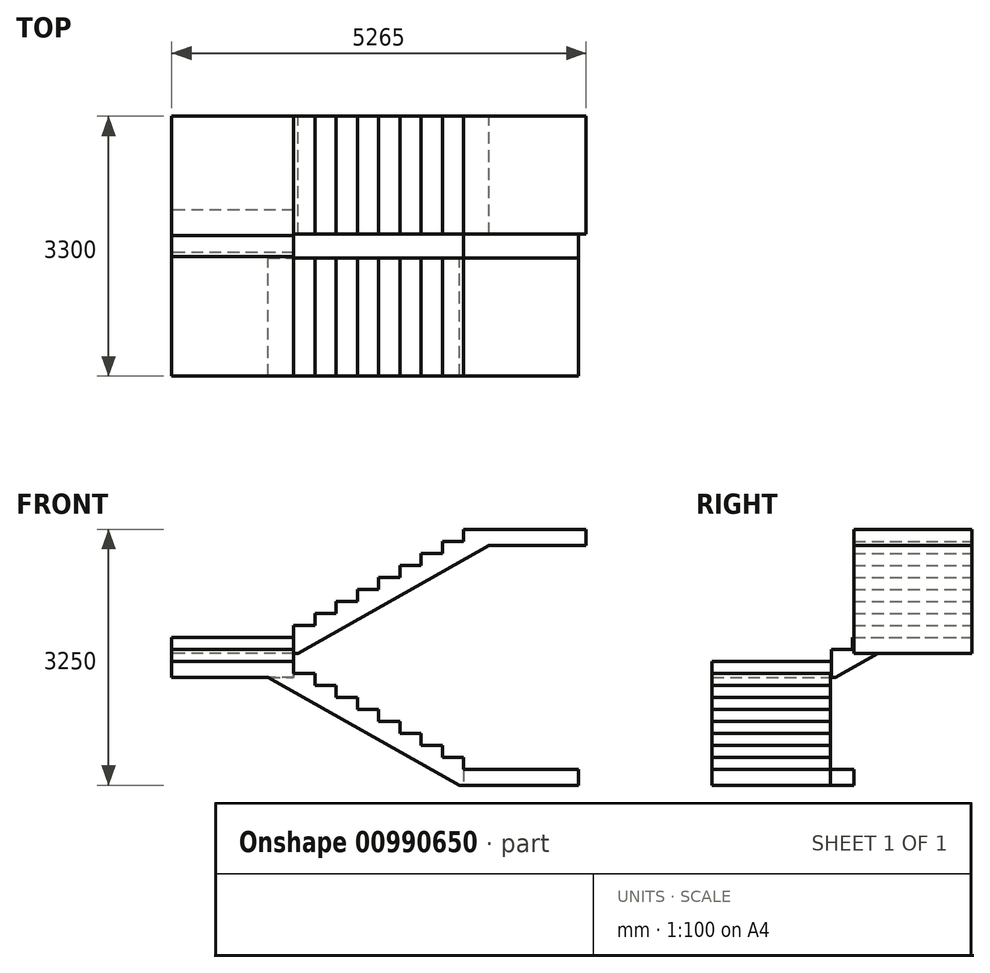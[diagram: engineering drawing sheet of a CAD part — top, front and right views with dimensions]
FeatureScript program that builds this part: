
annotation { "Feature Type Name" : "Feature", "Feature Type Description" : "" }
export const myFeature = defineFeature(function(context is Context, id is Id, definition is map)
    precondition{}
    {
        {
            var Q0;
            Q0=qCreatedBy(makeId("Front.planeOp"),FACE);
            var sketch = newSketch(context, id + "F0", { "sketchPlane" : qUnion([Q0])});
            skLineSegment(sketch, "E0", {"start": v(-2899.3, -2094.7) * mm, "end": v(-1349.3, -2094.7) * mm});
            skLineSegment(sketch, "E1", {"start": v(-1349.3, -2094.7) * mm, "end": v(-1349.3, -2247.2) * mm});
            skLineSegment(sketch, "E2", {"start": v(-1349.3, -2247.2) * mm, "end": v(-1079.3, -2247.2) * mm});
            skLineSegment(sketch, "E3", {"start": v(-1079.3, -2247.2) * mm, "end": v(-1079.3, -2399.7) * mm});
            skLineSegment(sketch, "E4", {"start": v(-1079.3, -2399.7) * mm, "end": v(-809.3, -2399.7) * mm});
            skLineSegment(sketch, "E5", {"start": v(-809.3, -2399.7) * mm, "end": v(-809.3, -2552.2) * mm});
            skLineSegment(sketch, "E6", {"start": v(-809.3, -2552.2) * mm, "end": v(-539.3, -2552.2) * mm});
            skLineSegment(sketch, "E7", {"start": v(-539.3, -2552.2) * mm, "end": v(-539.3, -2704.7) * mm});
            skLineSegment(sketch, "E8", {"start": v(-539.3, -2704.7) * mm, "end": v(-269.3, -2704.7) * mm});
            skLineSegment(sketch, "E9", {"start": v(-269.3, -2704.7) * mm, "end": v(-269.3, -2857.2) * mm});
            skLineSegment(sketch, "E10", {"start": v(-269.3, -2857.2) * mm, "end": v(0.7, -2857.2) * mm});
            skLineSegment(sketch, "E11", {"start": v(0.7, -2857.2) * mm, "end": v(0.7, -3009.7) * mm});
            skLineSegment(sketch, "E12", {"start": v(0.7, -3009.7) * mm, "end": v(270.7, -3009.7) * mm});
            skLineSegment(sketch, "E13", {"start": v(270.7, -3009.7) * mm, "end": v(270.7, -3162.2) * mm});
            skLineSegment(sketch, "E14", {"start": v(270.7, -3162.2) * mm, "end": v(540.7, -3162.2) * mm});
            skLineSegment(sketch, "E15", {"start": v(540.7, -3162.2) * mm, "end": v(540.7, -3314.7) * mm});
            skLineSegment(sketch, "E16", {"start": v(540.7, -3314.7) * mm, "end": v(810.7, -3314.7) * mm});
            skLineSegment(sketch, "E17", {"start": v(810.7, -3314.7) * mm, "end": v(810.7, -3467.2) * mm});
            skLineSegment(sketch, "E18", {"start": v(810.7, -3467.2) * mm, "end": v(2265.7, -3467.2) * mm});
            skLineSegment(sketch, "E19", {"start": v(2265.7, -3467.2) * mm, "end": v(2265.7, -3667.2) * mm});
            skLineSegment(sketch, "E20", {"start": v(-2899.3, -2094.7) * mm, "end": v(-2899.3, -2294.7) * mm});
            skLineSegment(sketch, "E21.0", {"start": v(-1447.65, -2421.35) * mm, "end": v(712.35, -3641.35) * mm});
            skLineSegment(sketch, "E22", {"start": v(2265.7, -3667.2) * mm, "end": v(758.13, -3667.2) * mm});
            skLineSegment(sketch, "E23", {"start": v(-2899.3, -2294.7) * mm, "end": v(-1671.87, -2294.7) * mm});
            skLineSegment(sketch, "E24", {"start": v(-1447.65, -2421.35) * mm, "end": v(-1671.87, -2294.7) * mm});
            skLineSegment(sketch, "E25", {"start": v(712.35, -3641.35) * mm, "end": v(758.13, -3667.2) * mm});
            skSolve(sketch);
        }
        {
            var Q0;
            Q0=makeQuery(id+"F0.imprint","IMPRINT",FACE,{"disambiguationData":[TD([[makeQuery(id+"F0.imprint","IMPRINT",EDGE,{"derivedFrom":sQuery(id+"F0.wireOp",EDGE,"E0")}),-1.0]])]});
            extrude(context, id + "F1", {"entities" : qUnion([Q0]), "depth" : 1500 * mm, "offsetDistance" : 25 * mm});
        }
        {
            var Q0;
            Q0=makeQuery(id+"F1.opExtrude","CAP_FACE",FACE,{"disambiguationData":[OSD([sQuery(id+"F0.wireOp",EDGE,"E0"),sQuery(id+"F0.wireOp",EDGE,"E1"),sQuery(id+"F0.wireOp",EDGE,"E2"),sQuery(id+"F0.wireOp",EDGE,"E3"),sQuery(id+"F0.wireOp",EDGE,"E4"),sQuery(id+"F0.wireOp",EDGE,"E5"),sQuery(id+"F0.wireOp",EDGE,"E6"),sQuery(id+"F0.wireOp",EDGE,"E7"),sQuery(id+"F0.wireOp",EDGE,"E8"),sQuery(id+"F0.wireOp",EDGE,"E9"),sQuery(id+"F0.wireOp",EDGE,"E10"),sQuery(id+"F0.wireOp",EDGE,"E11"),sQuery(id+"F0.wireOp",EDGE,"E12"),sQuery(id+"F0.wireOp",EDGE,"E13"),sQuery(id+"F0.wireOp",EDGE,"E14"),sQuery(id+"F0.wireOp",EDGE,"E15"),sQuery(id+"F0.wireOp",EDGE,"E16"),sQuery(id+"F0.wireOp",EDGE,"E17"),sQuery(id+"F0.wireOp",EDGE,"E18"),sQuery(id+"F0.wireOp",EDGE,"E19"),sQuery(id+"F0.wireOp",EDGE,"E20"),sQuery(id+"F0.wireOp",EDGE,"E21.0"),sQuery(id+"F0.wireOp",EDGE,"E22"),sQuery(id+"F0.wireOp",EDGE,"E23"),sQuery(id+"F0.wireOp",EDGE,"E24"),sQuery(id+"F0.wireOp",EDGE,"E25")])],"isStart":true});
            var sketch = newSketch(context, id + "F2", { "sketchPlane" : qUnion([Q0])});
            skLineSegment(sketch, "E26", {"start": v(1671.87, -2294.7) * mm, "end": v(1349.3, -2294.7) * mm});
            skLineSegment(sketch, "E27", {"start": v(1349.3, -2294.7) * mm, "end": v(1349.3, -2247.2) * mm});
            skLineSegment(sketch, "E28", {"start": v(1349.3, -2247.2) * mm, "end": v(1349.3, -2094.7) * mm});
            skLineSegment(sketch, "E29", {"start": v(1349.3, -2094.7) * mm, "end": v(2899.3, -2094.7) * mm});
            skLineSegment(sketch, "E30", {"start": v(2899.3, -2094.7) * mm, "end": v(2899.3, -2294.7) * mm});
            skLineSegment(sketch, "E31", {"start": v(2899.3, -2294.7) * mm, "end": v(1671.87, -2294.7) * mm});
            skSolve(sketch);
        }
        {
            var Q0;
            Q0=makeQuery(id+"F2.imprint","IMPRINT",FACE,{"disambiguationData":[TD([[makeQuery(id+"F2.imprint","IMPRINT",EDGE,{"derivedFrom":sQuery(id+"F2.wireOp",EDGE,"E26")}),-1.0]])]});
            extrude(context, id + "F3", {"entities" : qUnion([Q0]), "operationType" : NewBodyOperationType.ADD, "depth" : 15 * mm, "offsetDistance" : 25 * mm});
        }
        {
            var Q0;
            Q0=makeQuery(id+"F3.boolean.opBoolean","MERGE",FACE,{"derivedFrom":[makeQuery(id+"F1.opExtrude","SWEPT_FACE",FACE,{"disambiguationData":[OSD([sQuery(id+"F0.wireOp",EDGE,"E20")])]}),makeQuery(id+"F3.opExtrude","SWEPT_FACE",FACE,{"disambiguationData":[OSD([sQuery(id+"F2.wireOp",EDGE,"E30")])]})]});
            var sketch = newSketch(context, id + "F4", { "sketchPlane" : qUnion([Q0])});
            skLineSegment(sketch, "E32", {"start": v(-15, -2094.7) * mm, "end": v(-15, -1942.2) * mm});
            skLineSegment(sketch, "E33", {"start": v(-15, -1942.2) * mm, "end": v(-285, -1942.2) * mm});
            skLineSegment(sketch, "E34", {"start": v(-285, -1942.2) * mm, "end": v(-285, -1789.7) * mm});
            skLineSegment(sketch, "E35", {"start": v(-285, -1789.7) * mm, "end": v(-1800, -1789.7) * mm});
            skLineSegment(sketch, "E36", {"start": v(-1800, -1789.7) * mm, "end": v(-1800, -1989.7) * mm});
            skLineSegment(sketch, "E37", {"start": v(-1800, -1989.7) * mm, "end": v(-607.58, -1989.7) * mm});
            skLineSegment(sketch, "E38.0", {"start": v(-67.58, -2294.7) * mm, "end": v(-607.58, -1989.7) * mm});
            skLineSegment(sketch, "E39", {"start": v(-15, -2094.7) * mm, "end": v(-15, -2294.7) * mm});
            skLineSegment(sketch, "E40", {"start": v(-15, -2294.7) * mm, "end": v(-67.58, -2294.7) * mm});
            skSolve(sketch);
        }
        {
            var Q0;
            Q0=makeQuery(id+"F4.imprint","IMPRINT",FACE,{"disambiguationData":[TD([[makeQuery(id+"F4.imprint","IMPRINT",EDGE,{"derivedFrom":sQuery(id+"F4.wireOp",EDGE,"E32")}),1.0]])]});
            extrude(context, id + "F5", {"entities" : qUnion([Q0]), "oppositeDirection" : true, "depth" : 1550 * mm, "offsetDistance" : 25 * mm});
        }
        {
            var Q0;
            Q0=makeQuery(id+"F5.opExtrude","SWEPT_FACE",FACE,{"disambiguationData":[OSD([sQuery(id+"F4.wireOp",EDGE,"E36")])]});
            var sketch = newSketch(context, id + "F6", { "sketchPlane" : qUnion([Q0])});
            skLineSegment(sketch, "E41", {"start": v(1349.3, -1789.7) * mm, "end": v(1349.3, -1637.2) * mm});
            skLineSegment(sketch, "E42", {"start": v(1349.3, -1637.2) * mm, "end": v(1079.3, -1637.2) * mm});
            skLineSegment(sketch, "E43", {"start": v(1079.3, -1637.2) * mm, "end": v(1079.3, -1484.7) * mm});
            skLineSegment(sketch, "E44", {"start": v(1079.3, -1484.7) * mm, "end": v(809.3, -1484.7) * mm});
            skLineSegment(sketch, "E45", {"start": v(809.3, -1484.7) * mm, "end": v(809.3, -1332.2) * mm});
            skLineSegment(sketch, "E46", {"start": v(809.3, -1332.2) * mm, "end": v(539.3, -1332.2) * mm});
            skLineSegment(sketch, "E47", {"start": v(539.3, -1332.2) * mm, "end": v(539.3, -1179.7) * mm});
            skLineSegment(sketch, "E48", {"start": v(539.3, -1179.7) * mm, "end": v(269.3, -1179.7) * mm});
            skLineSegment(sketch, "E49", {"start": v(269.3, -1179.7) * mm, "end": v(269.3, -1027.2) * mm});
            skLineSegment(sketch, "E50", {"start": v(269.3, -1027.2) * mm, "end": v(-0.7, -1027.2) * mm});
            skLineSegment(sketch, "E51", {"start": v(-0.7, -1027.2) * mm, "end": v(-0.7, -874.7) * mm});
            skLineSegment(sketch, "E52", {"start": v(-0.7, -874.7) * mm, "end": v(-270.7, -874.7) * mm});
            skLineSegment(sketch, "E53", {"start": v(-270.7, -874.7) * mm, "end": v(-270.7, -722.2) * mm});
            skLineSegment(sketch, "E54", {"start": v(-270.7, -722.2) * mm, "end": v(-540.7, -722.2) * mm});
            skLineSegment(sketch, "E55", {"start": v(-540.7, -722.2) * mm, "end": v(-540.7, -569.7) * mm});
            skLineSegment(sketch, "E56", {"start": v(-540.7, -569.7) * mm, "end": v(-810.7, -569.7) * mm});
            skLineSegment(sketch, "E57", {"start": v(-810.7, -569.7) * mm, "end": v(-810.7, -417.2) * mm});
            skLineSegment(sketch, "E58", {"start": v(-810.7, -417.2) * mm, "end": v(-2365.7, -417.2) * mm});
            skLineSegment(sketch, "E59", {"start": v(-2365.7, -417.2) * mm, "end": v(-2365.7, -617.2) * mm});
            skLineSegment(sketch, "E60.0", {"start": v(1296.71, -1989.7) * mm, "end": v(-1133.29, -617.2) * mm});
            skLineSegment(sketch, "E61", {"start": v(-2365.7, -617.2) * mm, "end": v(-1133.29, -617.2) * mm});
            skLineSegment(sketch, "E62", {"start": v(1349.3, -1989.7) * mm, "end": v(1296.71, -1989.7) * mm});
            skLineSegment(sketch, "E63", {"start": v(1349.3, -1789.7) * mm, "end": v(1349.3, -1989.7) * mm});
            skSolve(sketch);
        }
        {
            var Q0;
            Q0=makeQuery(id+"F6.imprint","IMPRINT",FACE,{"disambiguationData":[TD([[makeQuery(id+"F6.imprint","IMPRINT",EDGE,{"derivedFrom":sQuery(id+"F6.wireOp",EDGE,"E41")}),1.0]])]});
            extrude(context, id + "F7", {"entities" : qUnion([Q0]), "oppositeDirection" : true, "depth" : 1500 * mm, "offsetDistance" : 25 * mm});
        }
        {
            var Q0;
            Q0=makeQuery(id+"F1.opExtrude","CAP_FACE",FACE,{"disambiguationData":[OSD([sQuery(id+"F0.wireOp",EDGE,"E0"),sQuery(id+"F0.wireOp",EDGE,"E1"),sQuery(id+"F0.wireOp",EDGE,"E2"),sQuery(id+"F0.wireOp",EDGE,"E3"),sQuery(id+"F0.wireOp",EDGE,"E4"),sQuery(id+"F0.wireOp",EDGE,"E5"),sQuery(id+"F0.wireOp",EDGE,"E6"),sQuery(id+"F0.wireOp",EDGE,"E7"),sQuery(id+"F0.wireOp",EDGE,"E8"),sQuery(id+"F0.wireOp",EDGE,"E9"),sQuery(id+"F0.wireOp",EDGE,"E10"),sQuery(id+"F0.wireOp",EDGE,"E11"),sQuery(id+"F0.wireOp",EDGE,"E12"),sQuery(id+"F0.wireOp",EDGE,"E13"),sQuery(id+"F0.wireOp",EDGE,"E14"),sQuery(id+"F0.wireOp",EDGE,"E15"),sQuery(id+"F0.wireOp",EDGE,"E16"),sQuery(id+"F0.wireOp",EDGE,"E17"),sQuery(id+"F0.wireOp",EDGE,"E18"),sQuery(id+"F0.wireOp",EDGE,"E19"),sQuery(id+"F0.wireOp",EDGE,"E20"),sQuery(id+"F0.wireOp",EDGE,"E21.0"),sQuery(id+"F0.wireOp",EDGE,"E22"),sQuery(id+"F0.wireOp",EDGE,"E23"),sQuery(id+"F0.wireOp",EDGE,"E24"),sQuery(id+"F0.wireOp",EDGE,"E25")])],"isStart":true});
            var sketch = newSketch(context, id + "F8", { "sketchPlane" : qUnion([Q0])});
            skLineSegment(sketch, "E64.bottom", {"start": v(-810.7, -3467.2) * mm, "end": v(-2265.7, -3467.2) * mm});
            skLineSegment(sketch, "E64.top", {"start": v(-810.7, -3667.2) * mm, "end": v(-2265.7, -3667.2) * mm});
            skLineSegment(sketch, "E64.left", {"start": v(-810.7, -3467.2) * mm, "end": v(-810.7, -3667.2) * mm});
            skLineSegment(sketch, "E64.right", {"start": v(-2265.7, -3467.2) * mm, "end": v(-2265.7, -3667.2) * mm});
            skSolve(sketch);
        }
        {
            var Q0;
            Q0=makeQuery(id+"F8.imprint","IMPRINT",FACE,{"disambiguationData":[TD([[makeQuery(id+"F8.imprint","IMPRINT",EDGE,{"derivedFrom":sQuery(id+"F8.wireOp",EDGE,"E64.bottom")}),1.0]])]});
            extrude(context, id + "F9", {"entities" : qUnion([Q0]), "depth" : 300 * mm, "offsetDistance" : 25 * mm});
        }
    });
